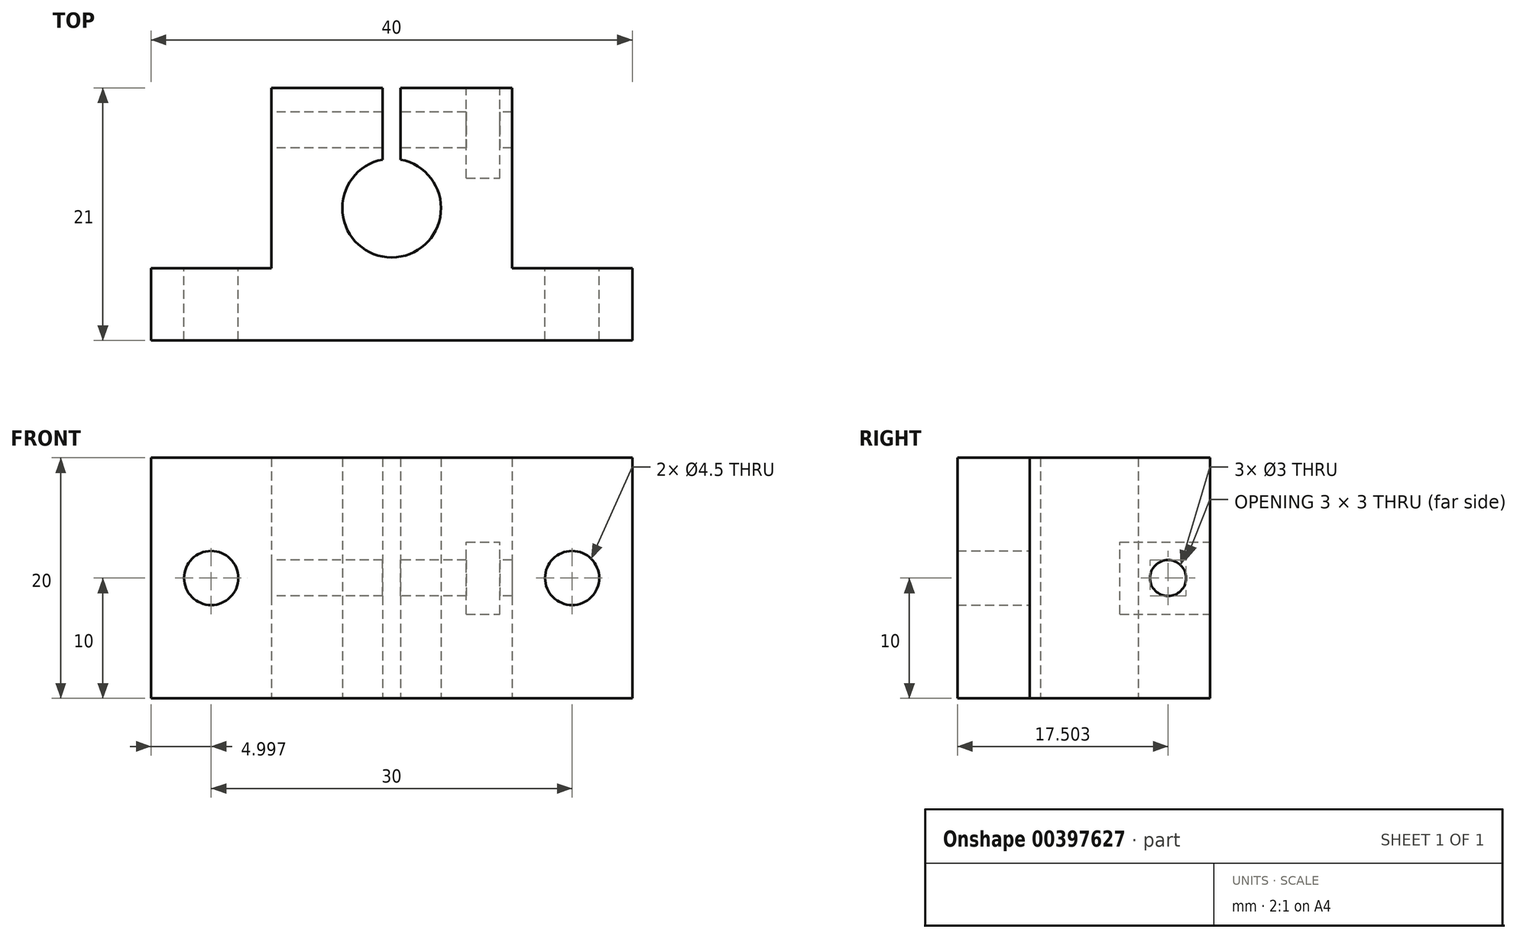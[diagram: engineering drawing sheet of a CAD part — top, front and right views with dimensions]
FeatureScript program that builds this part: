
annotation { "Feature Type Name" : "Feature", "Feature Type Description" : "" }
export const myFeature = defineFeature(function(context is Context, id is Id, definition is map)
    precondition{}
    {
        {
            var Q0;
            Q0=qCreatedBy(makeId("Top.planeOp"),FACE);
            var sketch = newSketch(context, id + "F0", { "sketchPlane" : qUnion([Q0])});
            skLineSegment(sketch, "E0.left", {"start": v(-48.33, -11.35) * mm, "end": v(-48.33, -5.35) * mm});
            skLineSegment(sketch, "E1.bottom", {"start": v(-38.33, -5.35) * mm, "end": v(-18.33, -5.35) * mm});
            skLineSegment(sketch, "E1.top", {"start": v(-38.33, 9.65) * mm, "end": v(-18.33, 9.65) * mm});
            skLineSegment(sketch, "E1.left", {"start": v(-38.33, -5.35) * mm, "end": v(-38.33, 9.65) * mm});
            skLineSegment(sketch, "E1.right", {"start": v(-18.33, -5.35) * mm, "end": v(-18.33, 9.65) * mm});
            skLineSegment(sketch, "E2", {"start": v(-8.33, -5.35) * mm, "end": v(-8.33, -11.35) * mm});
            skCircle(sketch, "E3", {"center": v(-28.33, -0.35) * mm, "radius": 4.1 * mm});
            skLineSegment(sketch, "E4.bottom", {"start": v(-29.08, 9.65) * mm, "end": v(-27.58, 9.65) * mm});
            skLineSegment(sketch, "E4.top", {"start": v(-29.08, -0.35) * mm, "end": v(-27.58, -0.35) * mm});
            skLineSegment(sketch, "E4.left", {"start": v(-29.08, 9.65) * mm, "end": v(-29.08, -0.35) * mm});
            skLineSegment(sketch, "E4.right", {"start": v(-27.58, 9.65) * mm, "end": v(-27.58, -0.35) * mm});
            skLineSegment(sketch, "E5", {"start": v(-48.33, -5.35) * mm, "end": v(-8.33, -5.35) * mm});
            skLineSegment(sketch, "E6", {"start": v(-8.33, -11.35) * mm, "end": v(-48.33, -11.35) * mm});
            skSolve(sketch);
        }
        {
            var Q0;
            {var subQ2=sQuery(id+"F0.wireOp",EDGE,"E1.left");Q0=makeQuery(id+"F0.imprint","IMPRINT",FACE,{"disambiguationData":[TD([[makeQuery(id+"F0.imprint","IMPRINT",EDGE,{"derivedFrom":subQ2}),-1.0]])]});}
            var Q1;
            {var subQ1=sQuery(id+"F0.wireOp",EDGE,"E0.left");Q1=makeQuery(id+"F0.imprint","IMPRINT",FACE,{"disambiguationData":[TD([[makeQuery(id+"F0.imprint","IMPRINT",EDGE,{"derivedFrom":subQ1}),-1.0]])]});}
            extrude(context, id + "F1", {"entities" : qUnion([Q0, Q1]), "depth" : 20 * mm});
        }
        {
            var Q0;
            Q0=makeQuery(id+"F1.opExtrude","SWEPT_FACE",FACE,{"disambiguationData":[OSD([sQuery(id+"F0.wireOp",EDGE,"E1.left")])]});
            var sketch = newSketch(context, id + "F2", { "sketchPlane" : qUnion([Q0])});
            skCircle(sketch, "E7", {"center": v(-6.15, 10) * mm, "radius": 1.5 * mm});
            skSolve(sketch);
        }
        {
            var Q0;
            Q0 = qSketchRegion(id + "F2", true);
            extrude(context, id + "F3", {"entities" : qUnion([Q0]), "operationType" : NewBodyOperationType.REMOVE, "oppositeDirection" : true, "depth" : 20 * mm});
        }
        {
            var Q0;
            {var subQ0=sQuery(id+"F0.wireOp",EDGE,"E1.top");Q0=makeQuery(id+"F1.opExtrude","SWEPT_FACE",FACE,{"disambiguationData":[OSD([subQ0]),TDD([makeQuery(id+"F0.imprint","IMPRINT",EDGE,{"disambiguationData":[TD([[makeQuery(id+"F0.imprint","INTERSECT",VERTEX,{"derivedFrom":[subQ0,sQuery(id+"F0.wireOp",EDGE,"E1.left")]}),-1.0]])],"derivedFrom":subQ0})])]});}
            var sketch = newSketch(context, id + "F4", { "sketchPlane" : qUnion([Q0])});
            skLineSegment(sketch, "E8.bottom", {"start": v(22.13, 7) * mm, "end": v(19.33, 7) * mm});
            skLineSegment(sketch, "E8.top", {"start": v(22.13, 13) * mm, "end": v(19.33, 13) * mm});
            skLineSegment(sketch, "E8.left", {"start": v(22.13, 7) * mm, "end": v(22.13, 13) * mm});
            skLineSegment(sketch, "E8.right", {"start": v(19.33, 7) * mm, "end": v(19.33, 13) * mm});
            skSolve(sketch);
        }
        {
            var Q0;
            Q0 = qSketchRegion(id + "F4", true);
            extrude(context, id + "F5", {"entities" : qUnion([Q0]), "operationType" : NewBodyOperationType.REMOVE, "oppositeDirection" : true, "depth" : 7.5 * mm});
        }
        {
            var Q0;
            {var subQ0=sQuery(id+"F0.wireOp",EDGE,"E5");Q0=makeQuery(id+"F1.opExtrude","SWEPT_FACE",FACE,{"disambiguationData":[OSD([subQ0]),TDD([makeQuery(id+"F0.imprint","IMPRINT",EDGE,{"disambiguationData":[TD([[makeQuery(id+"F0.imprint","INTERSECT",VERTEX,{"derivedFrom":[sQuery(id+"F0.wireOp",EDGE,"E0.left"),subQ0]}),-1.0]])],"derivedFrom":subQ0})])]});}
            var sketch = newSketch(context, id + "F6", { "sketchPlane" : qUnion([Q0])});
            skCircle(sketch, "E9", {"center": v(43.33, 10) * mm, "radius": 2.25 * mm});
            skLineSegment(sketch, "E10", {"start": v(28.33, 0) * mm, "end": v(28.33, 13.82) * mm});
            skCircle(sketch, "E11.MirrorC", {"center": v(13.33, 10) * mm, "radius": 2.25 * mm});
            skSolve(sketch);
        }
        {
            var Q0;
            Q0 = qSketchRegion(id + "F6", true);
            extrude(context, id + "F7", {"entities" : qUnion([Q0]), "operationType" : NewBodyOperationType.REMOVE, "oppositeDirection" : true, "depth" : 6 * mm});
        }
    });
